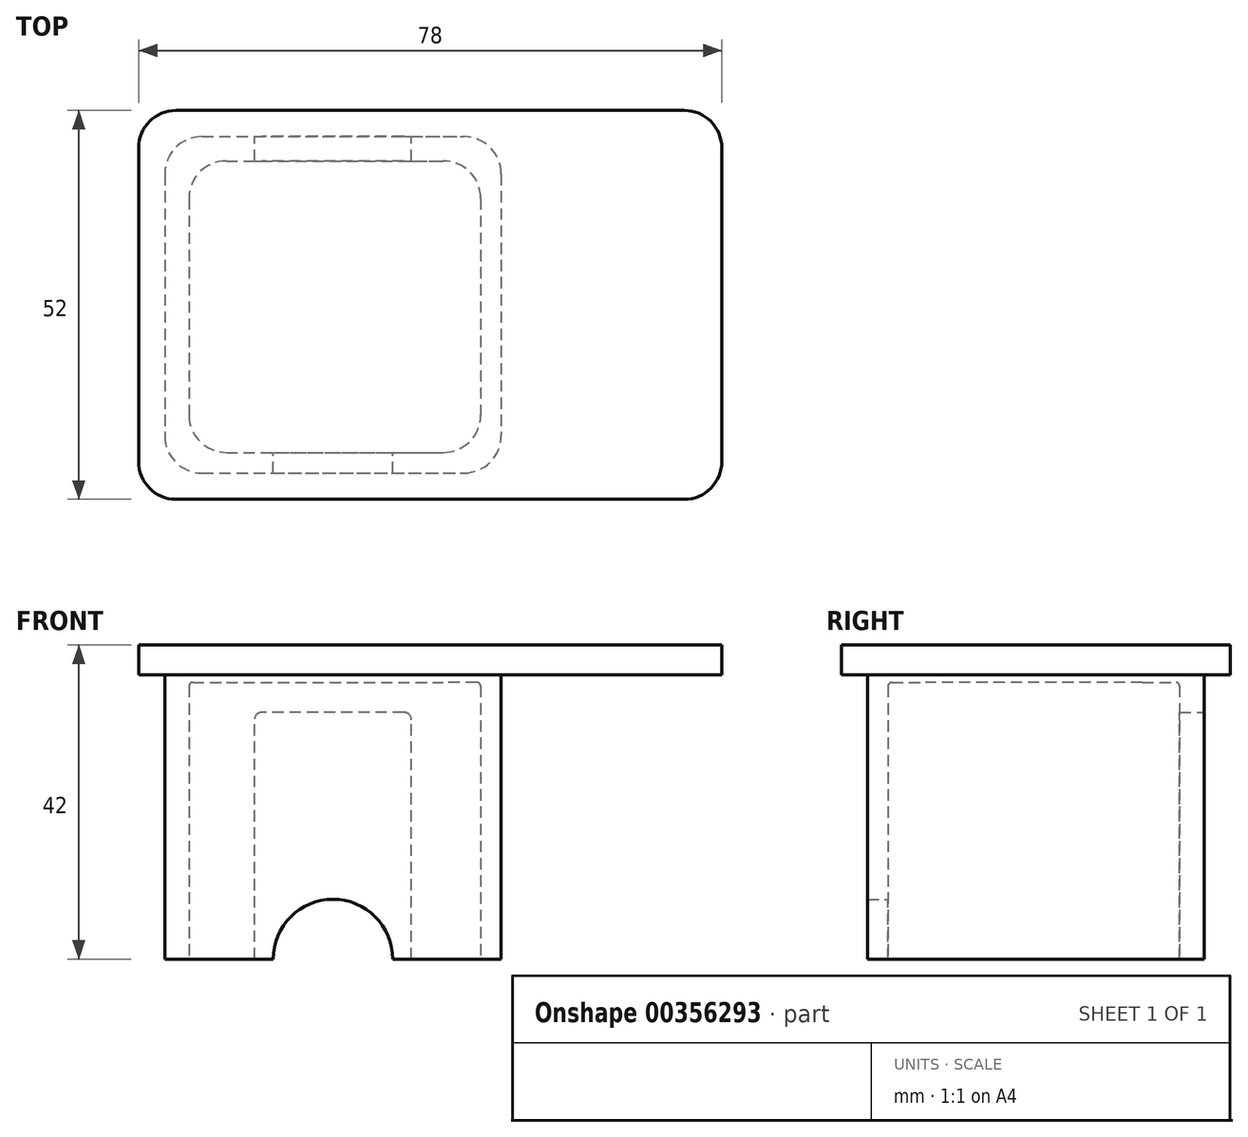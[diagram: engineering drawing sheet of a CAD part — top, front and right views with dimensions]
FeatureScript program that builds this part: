
annotation { "Feature Type Name" : "Feature", "Feature Type Description" : "" }
export const myFeature = defineFeature(function(context is Context, id is Id, definition is map)
    precondition{}
    {
        {
            var Q0;
            Q0=qCreatedBy(makeId("Top.planeOp"),FACE);
            var sketch = newSketch(context, id + "F0", { "sketchPlane" : qUnion([Q0])});
            skLineSegment(sketch, "E0.bottom", {"start": v(12.75, -2) * mm, "end": v(51.75, -2) * mm});
            skLineSegment(sketch, "E0.top", {"start": v(12.75, -41) * mm, "end": v(51.75, -41) * mm});
            skLineSegment(sketch, "E0.left", {"start": v(12.75, -2) * mm, "end": v(12.75, -41) * mm});
            skLineSegment(sketch, "E0.right", {"start": v(51.75, -2) * mm, "end": v(51.75, -41) * mm});
            skSolve(sketch);
        }
        {
            var Q0;
            Q0=qCreatedBy(makeId("Top.planeOp"),FACE);
            var sketch = newSketch(context, id + "F1", { "sketchPlane" : qUnion([Q0])});
            skLineSegment(sketch, "E1.bottom", {"start": v(9.5, 1.25) * mm, "end": v(54.5, 1.25) * mm});
            skLineSegment(sketch, "E1.top", {"start": v(9.5, -43.75) * mm, "end": v(54.5, -43.75) * mm});
            skLineSegment(sketch, "E1.left", {"start": v(9.5, 1.25) * mm, "end": v(9.5, -43.75) * mm});
            skLineSegment(sketch, "E1.right", {"start": v(54.5, 1.25) * mm, "end": v(54.5, -43.75) * mm});
            skPoint(sketch, "E2", {"position": v(32, -21.25) * mm});
            skPoint(sketch, "E2.positionSnap0", {"position": v(9.5, -21.25) * mm});
            skPoint(sketch, "E2.positionSnap1", {"position": v(32, 1.25) * mm});
            skSolve(sketch);
        }
        {
            var Q0;
            Q0=makeQuery(id+"F1.imprint","IMPRINT",FACE,{"disambiguationData":[TD([[makeQuery(id+"F1.imprint","IMPRINT",EDGE,{"derivedFrom":sQuery(id+"F1.wireOp",EDGE,"E1.bottom")}),-1.0]])]});
            extrude(context, id + "F2", {"entities" : qUnion([Q0]), "depth" : 38 * mm});
        }
        {
            var Q0;
            Q0=makeQuery(id+"F0.imprint","IMPRINT",FACE,{"disambiguationData":[TD([[makeQuery(id+"F0.imprint","IMPRINT",EDGE,{"derivedFrom":sQuery(id+"F0.wireOp",EDGE,"E0.bottom")}),-1.0]])]});
            extrude(context, id + "F3", {"entities" : qUnion([Q0]), "operationType" : NewBodyOperationType.REMOVE, "depth" : 37 * mm});
        }
        {
            var Q0;
            Q0=makeQuery(id+"F3.boolean.opBoolean","COPY",EDGE,{"derivedFrom":makeQuery(id+"F3.opExtrude","SWEPT_EDGE",EDGE,{"disambiguationData":[OSD([sQuery(id+"F0.wireOp",EDGE,"E0.top"),sQuery(id+"F0.wireOp",EDGE,"E0.left")])]})});
            var Q1;
            Q1=makeQuery(id+"F3.boolean.opBoolean","COPY",EDGE,{"derivedFrom":makeQuery(id+"F3.opExtrude","SWEPT_EDGE",EDGE,{"disambiguationData":[OSD([sQuery(id+"F0.wireOp",EDGE,"E0.top"),sQuery(id+"F0.wireOp",EDGE,"E0.right")])]})});
            var Q2;
            Q2=makeQuery(id+"F3.boolean.opBoolean","COPY",EDGE,{"derivedFrom":makeQuery(id+"F3.opExtrude","SWEPT_EDGE",EDGE,{"disambiguationData":[OSD([sQuery(id+"F0.wireOp",EDGE,"E0.bottom"),sQuery(id+"F0.wireOp",EDGE,"E0.right")])]})});
            var Q3;
            Q3=makeQuery(id+"F3.boolean.opBoolean","COPY",EDGE,{"derivedFrom":makeQuery(id+"F3.opExtrude","SWEPT_EDGE",EDGE,{"disambiguationData":[OSD([sQuery(id+"F0.wireOp",EDGE,"E0.bottom"),sQuery(id+"F0.wireOp",EDGE,"E0.left")])]})});
            fillet(context, id + "F4", {"entities" : qUnion([Q0, Q1, Q2, Q3]), "radius" : 5 * mm, "tangentPropagation" : true, "allowEdgeOverflow" : false});
        }
        {
            var Q0;
            Q0=makeQuery(id+"F3.boolean.opBoolean","COPY",EDGE,{"derivedFrom":makeQuery(id+"F3.opExtrude","CAP_EDGE",EDGE,{"disambiguationData":[OSD([sQuery(id+"F0.wireOp",EDGE,"E0.right")])],"isStart":false})});
            fillet(context, id + "F5", {"entities" : qUnion([Q0]), "radius" : .5 * mm, "tangentPropagation" : true, "allowEdgeOverflow" : false});
        }
        {
            var Q0;
            Q0=makeQuery(id+"F2.opExtrude","SWEPT_EDGE",EDGE,{"disambiguationData":[OSD([sQuery(id+"F1.wireOp",EDGE,"E1.bottom"),sQuery(id+"F1.wireOp",EDGE,"E1.right")])]});
            var Q1;
            Q1=makeQuery(id+"F2.opExtrude","SWEPT_EDGE",EDGE,{"disambiguationData":[OSD([sQuery(id+"F1.wireOp",EDGE,"E1.top"),sQuery(id+"F1.wireOp",EDGE,"E1.right")])]});
            var Q2;
            Q2=makeQuery(id+"F2.opExtrude","SWEPT_EDGE",EDGE,{"disambiguationData":[OSD([sQuery(id+"F1.wireOp",EDGE,"E1.top"),sQuery(id+"F1.wireOp",EDGE,"E1.left")])]});
            var Q3;
            Q3=makeQuery(id+"F2.opExtrude","SWEPT_EDGE",EDGE,{"disambiguationData":[OSD([sQuery(id+"F1.wireOp",EDGE,"E1.bottom"),sQuery(id+"F1.wireOp",EDGE,"E1.left")])]});
            fillet(context, id + "F6", {"entities" : qUnion([Q0, Q1, Q2, Q3]), "radius" : 5 * mm, "tangentPropagation" : true, "allowEdgeOverflow" : false});
        }
        {
            var Q0;
            Q0=makeQuery(id+"F2.opExtrude","SWEPT_FACE",FACE,{"disambiguationData":[OSD([sQuery(id+"F1.wireOp",EDGE,"E1.bottom")])]});
            var sketch = newSketch(context, id + "F7", { "sketchPlane" : qUnion([Q0])});
            skCircle(sketch, "E3", {"center": v(-32, 0) * mm, "radius": 8 * mm});
            skSolve(sketch);
        }
        {
            var Q0;
            Q0 = qSketchRegion(id + "F7", true);
            extrude(context, id + "F8", {"entities" : qUnion([Q0]), "operationType" : NewBodyOperationType.REMOVE, "endBound" : BoundingType.THROUGH_ALL, "oppositeDirection" : true, "depth" : 25 * mm});
        }
        {
            var Q0;
            Q0=makeQuery(id+"F2.opExtrude","CAP_FACE",FACE,{"disambiguationData":[OSD([sQuery(id+"F1.wireOp",EDGE,"E1.bottom"),sQuery(id+"F1.wireOp",EDGE,"E1.top"),sQuery(id+"F1.wireOp",EDGE,"E1.left"),sQuery(id+"F1.wireOp",EDGE,"E1.right")])],"isStart":false});
            var sketch = newSketch(context, id + "F9", { "sketchPlane" : qUnion([Q0])});
            skLineSegment(sketch, "E4.bottom", {"start": v(6, 4.75) * mm, "end": v(58, 4.75) * mm});
            skLineSegment(sketch, "E4.top", {"start": v(6, -47.25) * mm, "end": v(58, -47.25) * mm});
            skLineSegment(sketch, "E4.left", {"start": v(6, 4.75) * mm, "end": v(6, -47.25) * mm});
            skLineSegment(sketch, "E4.right", {"start": v(58, 4.75) * mm, "end": v(58, -47.25) * mm});
            skSolve(sketch);
        }
        {
            var Q0;
            Q0 = qSketchRegion(id + "F9", true);
            extrude(context, id + "F10", {"entities" : qUnion([Q0]), "operationType" : NewBodyOperationType.ADD, "depth" : 4 * mm});
        }
        {
            var Q0;
            Q0=makeQuery(id+"F10.opExtrude","SWEPT_EDGE",EDGE,{"disambiguationData":[OSD([sQuery(id+"F9.wireOp",EDGE,"E4.bottom"),sQuery(id+"F9.wireOp",EDGE,"E4.left")])]});
            var Q1;
            Q1=makeQuery(id+"F10.opExtrude","SWEPT_EDGE",EDGE,{"disambiguationData":[OSD([sQuery(id+"F9.wireOp",EDGE,"E4.bottom"),sQuery(id+"F9.wireOp",EDGE,"E4.right")])]});
            var Q2;
            Q2=makeQuery(id+"F10.opExtrude","SWEPT_EDGE",EDGE,{"disambiguationData":[OSD([sQuery(id+"F9.wireOp",EDGE,"E4.top"),sQuery(id+"F9.wireOp",EDGE,"E4.right")])]});
            var Q3;
            Q3=makeQuery(id+"F10.opExtrude","SWEPT_EDGE",EDGE,{"disambiguationData":[OSD([sQuery(id+"F9.wireOp",EDGE,"E4.top"),sQuery(id+"F9.wireOp",EDGE,"E4.left")])]});
            fillet(context, id + "F11", {"entities" : qUnion([Q0, Q1, Q2, Q3]), "radius" : 5 * mm, "tangentPropagation" : true, "allowEdgeOverflow" : false});
        }
        {
            var Q0;
            Q0=makeQuery(id+"F2.opExtrude","SWEPT_FACE",FACE,{"disambiguationData":[OSD([sQuery(id+"F1.wireOp",EDGE,"E1.bottom")])]});
            var sketch = newSketch(context, id + "F12", { "sketchPlane" : qUnion([Q0])});
            skLineSegment(sketch, "E5.bottom", {"start": v(-42.5, 0) * mm, "end": v(-21.5, 0) * mm});
            skLineSegment(sketch, "E5.top", {"start": v(-42.5, 33) * mm, "end": v(-21.5, 33) * mm});
            skLineSegment(sketch, "E5.left", {"start": v(-42.5, 0) * mm, "end": v(-42.5, 33) * mm});
            skLineSegment(sketch, "E5.right", {"start": v(-21.5, 0) * mm, "end": v(-21.5, 33) * mm});
            skPoint(sketch, "E5.middle", {"position": v(-32, 16.5) * mm});
            skPoint(sketch, "E5.middle.positionSnap0", {"position": v(-32, 8) * mm});
            skPoint(sketch, "E5.centerSnap0", {"position": v(-32, 8) * mm});
            skSolve(sketch);
        }
        {
            var Q0;
            Q0=makeQuery(id+"F12.imprint","IMPRINT",FACE,{"disambiguationData":[TD([[makeQuery(id+"F12.imprint","IMPRINT",EDGE,{"derivedFrom":sQuery(id+"F12.wireOp",EDGE,"E5.top")}),-1.0]])]});
            extrude(context, id + "F13", {"entities" : qUnion([Q0]), "operationType" : NewBodyOperationType.REMOVE, "oppositeDirection" : true, "depth" : 11.9 * mm});
        }
        {
            var Q0;
            Q0=makeQuery(id+"F13.boolean.opBoolean","COPY",EDGE,{"derivedFrom":makeQuery(id+"F13.opExtrude","SWEPT_EDGE",EDGE,{"disambiguationData":[OSD([sQuery(id+"F12.wireOp",EDGE,"E5.top"),sQuery(id+"F12.wireOp",EDGE,"E5.right")])]})});
            var Q1;
            Q1=makeQuery(id+"F13.boolean.opBoolean","COPY",EDGE,{"derivedFrom":makeQuery(id+"F13.opExtrude","SWEPT_EDGE",EDGE,{"disambiguationData":[OSD([sQuery(id+"F12.wireOp",EDGE,"E5.top"),sQuery(id+"F12.wireOp",EDGE,"E5.left")])]})});
            fillet(context, id + "F14", {"entities" : qUnion([Q0, Q1]), "radius" : 1 * mm, "tangentPropagation" : true, "allowEdgeOverflow" : false});
        }
        {
            var Q0;
            Q0=makeQuery(id+"F10.opExtrude","CAP_FACE",FACE,{"disambiguationData":[OSD([sQuery(id+"F9.wireOp",EDGE,"E4.bottom"),sQuery(id+"F9.wireOp",EDGE,"E4.top"),sQuery(id+"F9.wireOp",EDGE,"E4.left"),sQuery(id+"F9.wireOp",EDGE,"E4.right")])],"isStart":false});
            var sketch = newSketch(context, id + "F15", { "sketchPlane" : qUnion([Q0])});
            skSolve(sketch);
        }
        {
            var Q0;
            {var subQ3=sQuery(id+"F9.wireOp",EDGE,"E4.bottom");Q0=makeQuery(id+"F15.imprint","IMPRINT",FACE,{"disambiguationData":[TD([[makeQuery(id+"F15.imprint","IMPRINT",EDGE,{"derivedFrom":makeQuery(id+"F10.opExtrude","CAP_EDGE",EDGE,{"disambiguationData":[OSD([subQ3])],"isStart":false})}),-1.0]])]});}
            var sketch = newSketch(context, id + "F16", { "sketchPlane" : qUnion([Q0])});
            skLineSegment(sketch, "E6.bottom", {"start": v(53, 4.75) * mm, "end": v(84, 4.75) * mm});
            skLineSegment(sketch, "E6.top", {"start": v(53, -47.25) * mm, "end": v(84, -47.25) * mm});
            skLineSegment(sketch, "E6.left", {"start": v(53, 4.75) * mm, "end": v(53, -47.25) * mm});
            skLineSegment(sketch, "E6.right", {"start": v(84, 4.75) * mm, "end": v(84, -47.25) * mm});
            skSolve(sketch);
        }
        {
            var Q0;
            Q0 = qSketchRegion(id + "F16", true);
            extrude(context, id + "F17", {"entities" : qUnion([Q0]), "operationType" : NewBodyOperationType.ADD, "oppositeDirection" : true, "depth" : 4 * mm});
        }
        {
            var Q0;
            Q0=makeQuery(id+"F17.opExtrude","SWEPT_EDGE",EDGE,{"disambiguationData":[OSD([sQuery(id+"F16.wireOp",EDGE,"E6.bottom"),sQuery(id+"F16.wireOp",EDGE,"E6.right")])]});
            var Q1;
            Q1=makeQuery(id+"F17.opExtrude","SWEPT_EDGE",EDGE,{"disambiguationData":[OSD([sQuery(id+"F16.wireOp",EDGE,"E6.top"),sQuery(id+"F16.wireOp",EDGE,"E6.right")])]});
            fillet(context, id + "F18", {"entities" : qUnion([Q0, Q1]), "radius" : 5 * mm, "tangentPropagation" : true, "allowEdgeOverflow" : false});
        }
    });
